# Revit family: VENTS-VKO1
name_source: partatom
category: Mechanical Equipment
units: mm (PartAtom-declared; Revit-internal decimal feet)

## family parameters
Always vertical = Yes
Classification = None
Cut with Voids When Loaded = No
OmniClass Number = 23.75.35.17.11
OmniClass Title = Fans for Air Ductwork
Part Type = Breaks Into
Room Calculation Point = No
Round Connector Dimension = Use Diameter
Shared = No
Work Plane-Based = No

## types (3) — shared parameters
Casing Material = Plastic White Glazed
Current = 0 A
D1 = 59 mm
Description = Inline axial fan for round ducts
Family Version = 1.0
L1 = 28 mm  [stored 0.0918635 ft]
Load Classification = HVAC
Maintenance Zone Height = 600 mm
Maintenance Zone Length = 400 mm  [stored 1.31234 ft]
Maintenance Zone Material = Maintenance Zone
Maintenance Zone Width = 400 mm  [stored 1.31234 ft]
Manufacturer = Vents
Number of Poles = 1
Power Factor = 1
Protection rating = IPX4
Transported Air Temperature (°C) = +1...+40
URL = https://ventilation-system.com
Voltage = 230 V
dFl = 23 mm  [stored 0.0754593 ft]
sFl = 2 mm  [stored 0.00656168 ft]

## per-type parameters (varying)
| type | Apparent Power | Connection Diameter | D | L | Maximum Air Flow | Noise Level at 3 m (dBa) | Power | RPM (min-1) | Type Comments | Weight | gsD |
| 100 VKO1 | 14 VA | 100 mm  [stored 0.328084 ft] | 100 mm  [stored 0.328084 ft] | 85 mm  [stored 0.278871 ft] | 107 m³/h | 36 | 14 W | 2300 | Inline axial fan 100 VKO1 | 0.41 kg | 68 mm |
| 125 VKO1 | 16 VA | 125 mm  [stored 0.410105 ft] | 125 mm  [stored 0.410105 ft] | 90 mm  [stored 0.295276 ft] | 190 m³/h | 38 | 16 W | 2400 | Inline axial fan 125 VKO1 | 0.43 kg | 72 mm  [stored 0.23622 ft] |
| 150 VKO1 | 29 VA | 150 mm | 150 mm | 100 mm  [stored 0.328084 ft] | 305 m³/h | 40 | 29 W | 2400 | Inline axial fan 150 VKO1 | 0.80 kg | 80 mm  [stored 0.262467 ft] |

note: column(s) folded — value = type name in every type: Model

note: [stored X ft] marks values corroborated as IEEE doubles in the binary element streams (Revit-internal decimal feet)

## geometry (parser evidence)
native form markers: Sweep x7
no freeform markers — native parametric forms only
